# Revit family: FILTRATION ANTI-BACTERIENNE MURALE
name_source: partatom
category: Equipement de génie climatique
revit_build: Autodesk Revit 2018 (Build: 20170223_1515(x64)
units: mm (PartAtom-declared; Revit-internal decimal feet)

## family parameters
Basée sur le plan de construction = Non
Classification = Aucun
Cote de connecteur circulaire = Utiliser le diamètre
Couper avec des vides une fois chargée = Non
Partagée = Non
Point de calcul de pièce = Non
Toujours verticalement = Oui
Type d'élément = Normal

## types (5) — shared parameters
BRANCHEMENT_TERRE = Oui
DESCR_PIQUAGE = Prise info - Tuyau Rilsan Ø6
OFFSET_HAUT_CANA = 27 mm  [stored 0.0885827 ft]
OFFSET_HAUT_ZONE_MAINT = 264.5 mm  [stored 0.867782 ft]
ØPIQUAGE = 6 mm  [stored 0.019685 ft]
ØRACCORD = 32 mm  [stored 0.104987 ft]
zero-valued in all types: POIDS(Kg)

## per-type parameters (varying)
| type | DEBIT_MAX | DESCR_CONNECT | ENTRAXE_FILTRE | ENTRAXE_TE | Fabricant | HAUT_FILTRAT | HAUT_FILTRE | LONG. | OFFSET_LARG_CANA_1 | OFFSET_LARG_CANA_2 | OFFSET_MONTAGE | OFFSET_VANNE_1 | OFFSET_VANNE_2 | TYPE_EQUERRE_D | TYPE_EQUERRE_G | TYPE_FILTRE | TYPE_VANNE | ØCANA |
| c - FD260DP | 260.0 m³/h | G 1"1/4 - FEMELLE | 260 mm  [stored 0.853018 ft] | 710 mm |  | 571.5 mm  [stored 1.875 ft] | 307 mm  [stored 1.00722 ft] | 803 mm | 75 mm | 182.5 mm  [stored 0.598753 ft] | 400 mm  [stored 1.31234 ft] | 230 mm  [stored 0.754593 ft] | 40 mm  [stored 0.131234 ft] | EQUERRE SUPPORT : EQUERRE LONGUE | EQUERRE SUPPORT : EQUERRE COURTE | FILTRATION ANTI-BACTERIENNE : FD130 | Vanne BS FF : DN25 - G1" - FF (231 0001) | 35 mm  [stored 0.114829 ft] |
| a - FD60DP | 60.0 m³/h | G 3/4" - FEMELLE | 210 mm  [stored 0.688976 ft] | 558 mm |  | 440.5 mm  [stored 1.44521 ft] | 176 mm  [stored 0.577428 ft] | 624 mm  [stored 2.04724 ft] | 65 mm  [stored 0.213255 ft] | 144 mm  [stored 0.472441 ft] | 312 mm  [stored 1.02362 ft] | 180 mm  [stored 0.590551 ft] | 30 mm  [stored 0.0984252 ft] | EQUERRE SUPPORT : EQUERRE LONGUE 2 | EQUERRE SUPPORT : EQUERRE COURTE 2 | FILTRATION ANTI-BACTERIENNE : FD30 | Vanne BS FF : DN15 - G1/2" - FF (231 0002) | 20 mm  [stored 0.0656168 ft] |
| b - FD130DP | 130.0 m³/h | G 1" - FEMELLE | 260 mm  [stored 0.853018 ft] | 627 mm  [stored 2.05709 ft] |  | 564.5 mm  [stored 1.85203 ft] | 300 mm  [stored 0.984252 ft] | 705 mm  [stored 2.31299 ft] | 65 mm  [stored 0.213255 ft] | 156 mm  [stored 0.511811 ft] | 352.5 mm  [stored 1.1565 ft] | 200 mm  [stored 0.656168 ft] | 60 mm  [stored 0.19685 ft] | EQUERRE SUPPORT : EQUERRE LONGUE 3 | EQUERRE SUPPORT : EQUERRE COURTE 2 | FILTRATION ANTI-BACTERIENNE : FD65 | Vanne BS FF : DN15 - G1/2" - FF (231 0002) | 20 mm  [stored 0.0656168 ft] |
| d - FD640DP | 640.0 m³/h | G 2" - FEMELLE | 358 mm  [stored 1.17454 ft] | 938.5 mm |  | 609.5 mm | 345 mm  [stored 1.13189 ft] | 1055 mm | 120 mm  [stored 0.393701 ft] | 266 mm  [stored 0.872703 ft] | 527.5 mm  [stored 1.73064 ft] | 300 mm  [stored 0.984252 ft] | 60 mm  [stored 0.19685 ft] | EQUERRE SUPPORT : EQUERRE LONGUE 4 | EQUERRE SUPPORT : EQUERRE COURTE 3 | FILTRATION ANTI-BACTERIENNE : FD320 | Vanne BS FF : DN40 - G1"1/2 - FF (231 0009) | 40 mm  [stored 0.131234 ft] |
| e - FD1200DP | 1200.0 m³/h | G 2" - FEMELLE | 358 mm  [stored 1.17454 ft] | 938.5 mm | MIL'S | 906.5 mm | 642 mm  [stored 2.1063 ft] | 1055 mm | 120 mm  [stored 0.393701 ft] | 266 mm  [stored 0.872703 ft] | 527.5 mm  [stored 1.73064 ft] | 300 mm  [stored 0.984252 ft] | 60 mm  [stored 0.19685 ft] | EQUERRE SUPPORT : EQUERRE LONGUE 4 | EQUERRE SUPPORT : EQUERRE COURTE 3 | FILTRATION ANTI-BACTERIENNE : FD600 | Vanne BS FF : DN40 - G1"1/2 - FF (231 0009) | 40 mm  [stored 0.131234 ft] |

note: [stored X ft] marks values corroborated as IEEE doubles in the binary element streams (Revit-internal decimal feet)

## geometry (parser evidence)
native form markers: Sweep x4
no freeform markers — native parametric forms only
